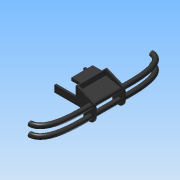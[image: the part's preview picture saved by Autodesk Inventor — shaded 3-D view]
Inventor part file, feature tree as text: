
AUTODESK INVENTOR PART (.ipt)
format: ipt  version: 2014 (Build 180170000, 170)  size: 292,352 bytes
history: native  units: in
note: dims shown in document units (in); Inventor stores cm internally (conversion verified against a paired STEP export)
features: sketch x9, extrude x5, mirror x2, plane x2, sweep x2, other x2, projected_geometry x1
ambient origin geometry x8: Origin, YZ Plane, XZ Plane, XY Plane, X Axis, Y Axis, Z Axis, Center Point
bodies: Solid1 (feature_tree)
feature tree (23):
  extrude  "Extrusion1"  Depth=2.4in TaperAngle=0.0deg
  extrude  "Extrusion2"  Depth=0.2in
  mirror  "Mirror1"
  extrude  "Extrusion3"  Depth=0.875in
  extrude  "Extrusion4"  Depth=0.2in
  sketch  "Sketch5"  dims[d10=1.975in d11=1.575in]
  plane  "Work Plane1"
  sweep  "Sweep1"
  sketch  "Sketch7"  dims[d14=0.16in d15=0.0in d16=0.1in d17=0.0in]
  plane  "Work Plane2"
  sweep  "Sweep2"
  mirror  "Mirror3"
  extrude  "Extrusion5"  Depth=0.1in TaperAngle=0.0deg
  sketch  "Sketch1"  dims[d0=0.42in d1=2.4in d2=0.0in]
  sketch  "Sketch2"  dims[d3=0.4in d4=0.2in]
  sketch  "Sketch3"  dims[d6=0.875in d7=0.6in]
  projected_geometry  "Projected Loop1"
  sketch  "Sketch4"  dims[d8=0.675in d9=0.2in]
  other  "Work Axis1"
  sketch  "Sketch6"  dims[d12=3.55in d13=1.0in]
  other  "Work Axis2"
  sketch  "Sketch8"  dims[d18=0.1in]
  sketch  "Sketch9"  dims[d20=0.1in d21=0.0in d22=0.46in d23=0.0in d24=0.0in d25=4.0in d27=0.0in d28=0.4835in d29=1.1997in d30=0.5in d31=4.0in d33=0.4835in d34=1.1997in d35=0.5in d36=0.0in d37=0.42in d38=0.26in d39=0.1in d40=0.1in d41=0.8in d42=0.0in d43=1.7in d44=1.7in]
